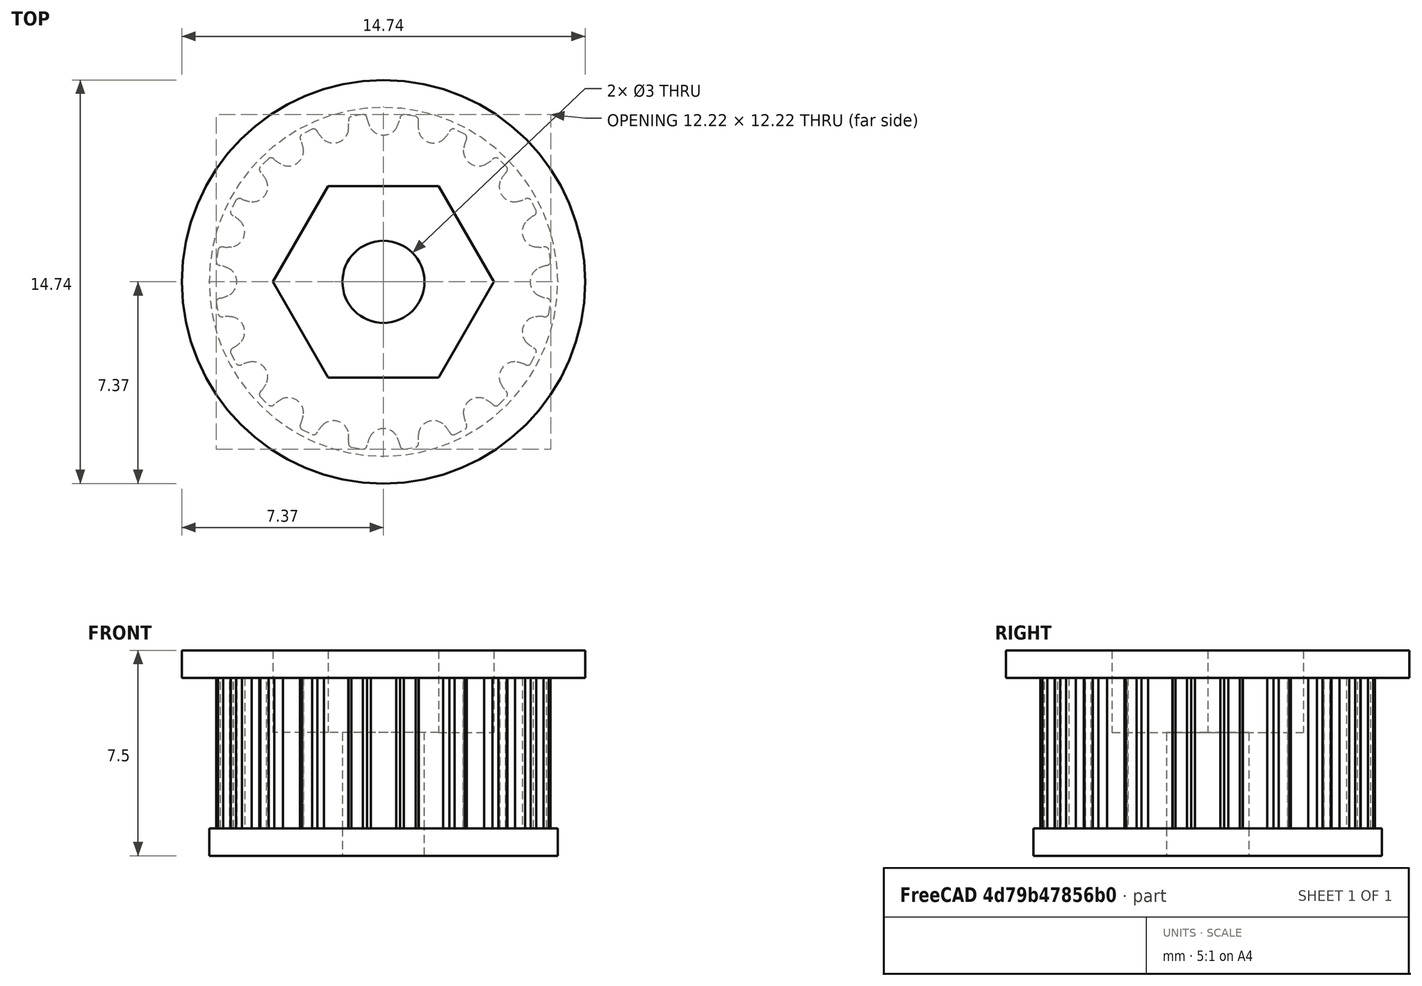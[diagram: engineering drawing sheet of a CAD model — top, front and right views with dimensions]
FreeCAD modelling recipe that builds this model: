
FCSTD DOCUMENT  (FreeCAD 0.18R16145 (Git))
Label: 20_tooth_GT2_M4_nut_hole
License: All rights reserved
LicenseURL: http://en.wikipedia.org/wiki/All_rights_reserved
objects: Sketcher::SketchObject×4, PartDesign::Pad×3, PartDesign::Pocket×1, PartDesign::Body×1
note: 13 computed .brp shape members not serialized (recipe doc carries the construction recipe); baked Part::Feature solids carry a one-line shape summary decoded from their .brp

FEATURE [Sketcher::SketchObject] SketchGear
  MapMode = 5
  Support = -> [XY_Plane]
  sketch-geometry (121):
    g0: ArcOfCircle CenterX=5.9622 CenterY=-0.75 CenterZ=0 NormalX=0 NormalY=0 NormalZ=1 AngleXU=8.1e-15 Radius=0.15 StartAngle=0 EndAngle=1.5708
    g1: ArcOfCircle CenterX=6.30816 CenterY=0.82798 CenterZ=0 NormalX=0 NormalY=0 NormalZ=-1 AngleXU=-1.3331 Radius=1.46929 StartAngle=0 EndAngle=0.255762
    g2: ArcOfCircle CenterX=5.92156 CenterY=0 CenterZ=0 NormalX=0 NormalY=0 NormalZ=-1 AngleXU=-0.984764 Radius=0.559359 StartAngle=0 EndAngle=1.96953
    g3: ArcOfCircle CenterX=6.30816 CenterY=-0.82798 CenterZ=0 NormalX=0 NormalY=0 NormalZ=-1 AngleXU=1.07734 Radius=1.46929 StartAngle=0 EndAngle=0.255762
    g4: ArcOfCircle CenterX=5.9622 CenterY=0.75 CenterZ=0 NormalX=0 NormalY=0 NormalZ=1 AngleXU=-1.5708 Radius=0.15 StartAngle=0 EndAngle=1.5708
    g5: LineSegment StartX=6.1122 StartY=0.75 StartZ=0 EndX=6.04481 EndY=1.17548 EndZ=0
    g6: ArcOfCircle CenterX=5.90215 CenterY=1.12913 CenterZ=0 NormalX=0 NormalY=0 NormalZ=1 AngleXU=0.314159 Radius=0.15 StartAngle=0 EndAngle=1.5708
    g7: ArcOfCircle CenterX=5.74356 CenterY=2.73679 CenterZ=0 NormalX=0 NormalY=0 NormalZ=-1 AngleXU=-1.64726 Radius=1.46929 StartAngle=0 EndAngle=0.255762
    g8: ArcOfCircle CenterX=5.63174 CenterY=1.82986 CenterZ=0 NormalX=0 NormalY=0 NormalZ=-1 AngleXU=-1.29892 Radius=0.559359 StartAngle=0 EndAngle=1.96953
    g9: ArcOfCircle CenterX=6.25528 CenterY=1.16187 CenterZ=0 NormalX=0 NormalY=0 NormalZ=-1 AngleXU=0.763178 Radius=1.46929 StartAngle=0 EndAngle=0.255762
    g10: ArcOfCircle CenterX=5.43862 CenterY=2.55571 CenterZ=0 NormalX=0 NormalY=0 NormalZ=1 AngleXU=-1.25664 Radius=0.15 StartAngle=0 EndAngle=1.5708
    g11: LineSegment StartX=5.58128 StartY=2.60207 StartZ=0 EndX=5.38571 EndY=2.9859 EndZ=0
    g12: ArcOfCircle CenterX=5.26436 CenterY=2.89773 CenterZ=0 NormalX=0 NormalY=0 NormalZ=1 AngleXU=0.628319 Radius=0.15 StartAngle=0 EndAngle=1.5708
    g13: ArcOfCircle CenterX=4.61674 CenterY=4.3777 CenterZ=0 NormalX=0 NormalY=0 NormalZ=-1 AngleXU=-1.96142 Radius=1.46929 StartAngle=0 EndAngle=0.255762
    g14: ArcOfCircle CenterX=4.79064 CenterY=3.4806 CenterZ=0 NormalX=0 NormalY=0 NormalZ=-1 AngleXU=-1.61308 Radius=0.559359 StartAngle=0 EndAngle=1.96953
    g15: ArcOfCircle CenterX=5.59009 CenterY=3.038 CenterZ=0 NormalX=0 NormalY=0 NormalZ=-1 AngleXU=0.449019 Radius=1.46929 StartAngle=0 EndAngle=0.255762
    g16: ArcOfCircle CenterX=4.38268 CenterY=4.11125 CenterZ=0 NormalX=0 NormalY=0 NormalZ=1 AngleXU=-0.942478 Radius=0.15 StartAngle=0 EndAngle=1.5708
    g17: LineSegment StartX=4.50403 StartY=4.19942 StartZ=0 EndX=4.19942 EndY=4.50403 EndZ=0
    g18: ArcOfCircle CenterX=4.11125 CenterY=4.38268 CenterZ=0 NormalX=0 NormalY=0 NormalZ=1 AngleXU=0.942478 Radius=0.15 StartAngle=0 EndAngle=1.5708
    g19: ArcOfCircle CenterX=3.038 CenterY=5.59009 CenterZ=0 NormalX=0 NormalY=0 NormalZ=-1 AngleXU=-2.27558 Radius=1.46929 StartAngle=0 EndAngle=0.255762
    g20: ArcOfCircle CenterX=3.4806 CenterY=4.79064 CenterZ=0 NormalX=0 NormalY=0 NormalZ=-1 AngleXU=-1.92724 Radius=0.559359 StartAngle=0 EndAngle=1.96953
    g21: ArcOfCircle CenterX=4.3777 CenterY=4.61674 CenterZ=0 NormalX=0 NormalY=0 NormalZ=-1 AngleXU=0.13486 Radius=1.46929 StartAngle=0 EndAngle=0.255762
    g22: ArcOfCircle CenterX=2.89773 CenterY=5.26436 CenterZ=0 NormalX=0 NormalY=0 NormalZ=1 AngleXU=-0.628319 Radius=0.15 StartAngle=0 EndAngle=1.5708
    g23: LineSegment StartX=2.9859 StartY=5.38571 StartZ=0 EndX=2.60207 EndY=5.58128 EndZ=0
    g24: ArcOfCircle CenterX=2.55571 CenterY=5.43862 CenterZ=0 NormalX=0 NormalY=0 NormalZ=1 AngleXU=1.25664 Radius=0.15 StartAngle=0 EndAngle=1.5708
    g25: ArcOfCircle CenterX=1.16187 CenterY=6.25528 CenterZ=0 NormalX=0 NormalY=0 NormalZ=-1 AngleXU=-2.58974 Radius=1.46929 StartAngle=0 EndAngle=0.255762
    g26: ArcOfCircle CenterX=1.82986 CenterY=5.63174 CenterZ=0 NormalX=0 NormalY=0 NormalZ=-1 AngleXU=-2.2414 Radius=0.559359 StartAngle=0 EndAngle=1.96953
    g27: ArcOfCircle CenterX=2.73679 CenterY=5.74356 CenterZ=0 NormalX=0 NormalY=0 NormalZ=-1 AngleXU=-0.1793 Radius=1.46929 StartAngle=0 EndAngle=0.255762
    g28: ArcOfCircle CenterX=1.12913 CenterY=5.90215 CenterZ=0 NormalX=0 NormalY=0 NormalZ=1 AngleXU=-0.314159 Radius=0.15 StartAngle=0 EndAngle=1.5708
    g29: LineSegment StartX=1.17548 StartY=6.04481 StartZ=0 EndX=0.75 EndY=6.1122 EndZ=0
    g30: ArcOfCircle CenterX=0.75 CenterY=5.9622 CenterZ=0 NormalX=0 NormalY=0 NormalZ=1 AngleXU=1.5708 Radius=0.15 StartAngle=0 EndAngle=1.5708
    g31: ArcOfCircle CenterX=-0.82798 CenterY=6.30816 CenterZ=0 NormalX=0 NormalY=0 NormalZ=-1 AngleXU=-2.9039 Radius=1.46929 StartAngle=0 EndAngle=0.255762
    g32: ArcOfCircle CenterX=3e-16 CenterY=5.92156 CenterZ=0 NormalX=0 NormalY=0 NormalZ=-1 AngleXU=-2.55556 Radius=0.559359 StartAngle=0 EndAngle=1.96953
    g33: ArcOfCircle CenterX=0.82798 CenterY=6.30816 CenterZ=0 NormalX=0 NormalY=0 NormalZ=-1 AngleXU=-0.493459 Radius=1.46929 StartAngle=0 EndAngle=0.255762
    g34: ArcOfCircle CenterX=-0.75 CenterY=5.9622 CenterZ=0 NormalX=0 NormalY=0 NormalZ=1 AngleXU=5.9e-15 Radius=0.15 StartAngle=0 EndAngle=1.5708
    g35: LineSegment StartX=-0.75 StartY=6.1122 StartZ=0 EndX=-1.17548 EndY=6.04481 EndZ=0
    g36: ArcOfCircle CenterX=-1.12913 CenterY=5.90215 CenterZ=0 NormalX=0 NormalY=0 NormalZ=1 AngleXU=1.88496 Radius=0.15 StartAngle=0 EndAngle=1.5708
    g37: ArcOfCircle CenterX=-2.73679 CenterY=5.74356 CenterZ=0 NormalX=0 NormalY=0 NormalZ=-1 AngleXU=3.06513 Radius=1.46929 StartAngle=0 EndAngle=0.255762
    g38: ArcOfCircle CenterX=-1.82986 CenterY=5.63174 CenterZ=0 NormalX=0 NormalY=0 NormalZ=-1 AngleXU=-2.86972 Radius=0.559359 StartAngle=0 EndAngle=1.96953
    g39: ArcOfCircle CenterX=-1.16187 CenterY=6.25528 CenterZ=0 NormalX=0 NormalY=0 NormalZ=-1 AngleXU=-0.807618 Radius=1.46929 StartAngle=0 EndAngle=0.255762
    g40: ArcOfCircle CenterX=-2.55571 CenterY=5.43862 CenterZ=0 NormalX=0 NormalY=0 NormalZ=1 AngleXU=0.314159 Radius=0.15 StartAngle=0 EndAngle=1.5708
    g41: LineSegment StartX=-2.60207 StartY=5.58128 StartZ=0 EndX=-2.9859 EndY=5.38571 EndZ=0
    g42: ArcOfCircle CenterX=-2.89773 CenterY=5.26436 CenterZ=0 NormalX=0 NormalY=0 NormalZ=1 AngleXU=2.19911 Radius=0.15 StartAngle=0 EndAngle=1.5708
    g43: ArcOfCircle CenterX=-4.3777 CenterY=4.61674 CenterZ=0 NormalX=0 NormalY=0 NormalZ=-1 AngleXU=2.75097 Radius=1.46929 StartAngle=0 EndAngle=0.255762
    g44: ArcOfCircle CenterX=-3.4806 CenterY=4.79064 CenterZ=0 NormalX=0 NormalY=0 NormalZ=-1 AngleXU=3.09931 Radius=0.559359 StartAngle=0 EndAngle=1.96953
    g45: ArcOfCircle CenterX=-3.038 CenterY=5.59009 CenterZ=0 NormalX=0 NormalY=0 NormalZ=-1 AngleXU=-1.12178 Radius=1.46929 StartAngle=0 EndAngle=0.255762
    g46: ArcOfCircle CenterX=-4.11125 CenterY=4.38268 CenterZ=0 NormalX=0 NormalY=0 NormalZ=1 AngleXU=0.628319 Radius=0.15 StartAngle=0 EndAngle=1.5708
    g47: LineSegment StartX=-4.19942 StartY=4.50403 StartZ=0 EndX=-4.50403 EndY=4.19942 EndZ=0
    g48: ArcOfCircle CenterX=-4.38268 CenterY=4.11125 CenterZ=0 NormalX=0 NormalY=0 NormalZ=1 AngleXU=2.51327 Radius=0.15 StartAngle=0 EndAngle=1.5708
    g49: ArcOfCircle CenterX=-5.59009 CenterY=3.038 CenterZ=0 NormalX=0 NormalY=0 NormalZ=-1 AngleXU=2.43681 Radius=1.46929 StartAngle=0 EndAngle=0.255762
    g50: ArcOfCircle CenterX=-4.79064 CenterY=3.4806 CenterZ=0 NormalX=0 NormalY=0 NormalZ=-1 AngleXU=2.78515 Radius=0.559359 StartAngle=0 EndAngle=1.96953
    g51: ArcOfCircle CenterX=-4.61674 CenterY=4.3777 CenterZ=0 NormalX=0 NormalY=0 NormalZ=-1 AngleXU=-1.43594 Radius=1.46929 StartAngle=0 EndAngle=0.255762
    g52: ArcOfCircle CenterX=-5.26436 CenterY=2.89773 CenterZ=0 NormalX=0 NormalY=0 NormalZ=1 AngleXU=0.942478 Radius=0.15 StartAngle=0 EndAngle=1.5708
    g53: LineSegment StartX=-5.38571 StartY=2.9859 StartZ=0 EndX=-5.58128 EndY=2.60207 EndZ=0
    g54: ArcOfCircle CenterX=-5.43862 CenterY=2.55571 CenterZ=0 NormalX=0 NormalY=0 NormalZ=1 AngleXU=2.82743 Radius=0.15 StartAngle=0 EndAngle=1.5708
    g55: ArcOfCircle CenterX=-6.25528 CenterY=1.16187 CenterZ=0 NormalX=0 NormalY=0 NormalZ=-1 AngleXU=2.12265 Radius=1.46929 StartAngle=0 EndAngle=0.255762
    g56: ArcOfCircle CenterX=-5.63174 CenterY=1.82986 CenterZ=0 NormalX=0 NormalY=0 NormalZ=-1 AngleXU=2.47099 Radius=0.559359 StartAngle=0 EndAngle=1.96953
    g57: ArcOfCircle CenterX=-5.74356 CenterY=2.73679 CenterZ=0 NormalX=0 NormalY=0 NormalZ=-1 AngleXU=-1.7501 Radius=1.46929 StartAngle=0 EndAngle=0.255762
    g58: ArcOfCircle CenterX=-5.90215 CenterY=1.12913 CenterZ=0 NormalX=0 NormalY=0 NormalZ=1 AngleXU=1.25664 Radius=0.15 StartAngle=0 EndAngle=1.5708
    g59: LineSegment StartX=-6.04481 StartY=1.17548 StartZ=0 EndX=-6.1122 EndY=0.75 EndZ=0
    g60: ArcOfCircle CenterX=-5.9622 CenterY=0.75 CenterZ=0 NormalX=0 NormalY=0 NormalZ=1 AngleXU=-3.14159 Radius=0.15 StartAngle=0 EndAngle=1.5708
    g61: ArcOfCircle CenterX=-6.30816 CenterY=-0.82798 CenterZ=0 NormalX=0 NormalY=0 NormalZ=-1 AngleXU=1.80849 Radius=1.46929 StartAngle=0 EndAngle=0.255762
    g62: ArcOfCircle CenterX=-5.92156 CenterY=7e-16 CenterZ=0 NormalX=0 NormalY=0 NormalZ=-1 AngleXU=2.15683 Radius=0.559359 StartAngle=0 EndAngle=1.96953
    g63: ArcOfCircle CenterX=-6.30816 CenterY=0.82798 CenterZ=0 NormalX=0 NormalY=0 NormalZ=-1 AngleXU=-2.06426 Radius=1.46929 StartAngle=0 EndAngle=0.255762
    g64: ArcOfCircle CenterX=-5.9622 CenterY=-0.75 CenterZ=0 NormalX=0 NormalY=0 NormalZ=1 AngleXU=1.5708 Radius=0.15 StartAngle=0 EndAngle=1.5708
    g65: LineSegment StartX=-6.1122 StartY=-0.75 StartZ=0 EndX=-6.04481 EndY=-1.17548 EndZ=0
    g66: ArcOfCircle CenterX=-5.90215 CenterY=-1.12913 CenterZ=0 NormalX=0 NormalY=0 NormalZ=1 AngleXU=-2.82743 Radius=0.15 StartAngle=0 EndAngle=1.5708
    g67: ArcOfCircle CenterX=-5.74356 CenterY=-2.73679 CenterZ=0 NormalX=0 NormalY=0 NormalZ=-1 AngleXU=1.49433 Radius=1.46929 StartAngle=0 EndAngle=0.255762
    g68: ArcOfCircle CenterX=-5.63174 CenterY=-1.82986 CenterZ=0 NormalX=0 NormalY=0 NormalZ=-1 AngleXU=1.84267 Radius=0.559359 StartAngle=0 EndAngle=1.96953
    g69: ArcOfCircle CenterX=-6.25528 CenterY=-1.16187 CenterZ=0 NormalX=0 NormalY=0 NormalZ=-1 AngleXU=-2.37841 Radius=1.46929 StartAngle=0 EndAngle=0.255762
    g70: ArcOfCircle CenterX=-5.43862 CenterY=-2.55571 CenterZ=0 NormalX=0 NormalY=0 NormalZ=1 AngleXU=1.88496 Radius=0.15 StartAngle=0 EndAngle=1.5708
    g71: LineSegment StartX=-5.58128 StartY=-2.60207 StartZ=0 EndX=-5.38571 EndY=-2.9859 EndZ=0
    g72: ArcOfCircle CenterX=-5.26436 CenterY=-2.89773 CenterZ=0 NormalX=0 NormalY=0 NormalZ=1 AngleXU=-2.51327 Radius=0.15 StartAngle=0 EndAngle=1.5708
    g73: ArcOfCircle CenterX=-4.61674 CenterY=-4.3777 CenterZ=0 NormalX=0 NormalY=0 NormalZ=-1 AngleXU=1.18017 Radius=1.46929 StartAngle=0 EndAngle=0.255762
    g74: ArcOfCircle CenterX=-4.79064 CenterY=-3.4806 CenterZ=0 NormalX=0 NormalY=0 NormalZ=-1 AngleXU=1.52851 Radius=0.559359 StartAngle=0 EndAngle=1.96953
    g75: ArcOfCircle CenterX=-5.59009 CenterY=-3.038 CenterZ=0 NormalX=0 NormalY=0 NormalZ=-1 AngleXU=-2.69257 Radius=1.46929 StartAngle=0 EndAngle=0.255762
    g76: ArcOfCircle CenterX=-4.38268 CenterY=-4.11125 CenterZ=0 NormalX=0 NormalY=0 NormalZ=1 AngleXU=2.19911 Radius=0.15 StartAngle=0 EndAngle=1.5708
    g77: LineSegment StartX=-4.50403 StartY=-4.19942 StartZ=0 EndX=-4.19942 EndY=-4.50403 EndZ=0
    g78: ArcOfCircle CenterX=-4.11125 CenterY=-4.38268 CenterZ=0 NormalX=0 NormalY=0 NormalZ=1 AngleXU=-2.19911 Radius=0.15 StartAngle=0 EndAngle=1.5708
    g79: ArcOfCircle CenterX=-3.038 CenterY=-5.59009 CenterZ=0 NormalX=0 NormalY=0 NormalZ=-1 AngleXU=0.866016 Radius=1.46929 StartAngle=0 EndAngle=0.255762
    g80: ArcOfCircle CenterX=-3.4806 CenterY=-4.79064 CenterZ=0 NormalX=0 NormalY=0 NormalZ=-1 AngleXU=1.21435 Radius=0.559359 StartAngle=0 EndAngle=1.96953
    g81: ArcOfCircle CenterX=-4.3777 CenterY=-4.61674 CenterZ=0 NormalX=0 NormalY=0 NormalZ=-1 AngleXU=-3.00673 Radius=1.46929 StartAngle=0 EndAngle=0.255762
    g82: ArcOfCircle CenterX=-2.89773 CenterY=-5.26436 CenterZ=0 NormalX=0 NormalY=0 NormalZ=1 AngleXU=2.51327 Radius=0.15 StartAngle=0 EndAngle=1.5708
    g83: LineSegment StartX=-2.9859 StartY=-5.38571 StartZ=0 EndX=-2.60207 EndY=-5.58128 EndZ=0
    g84: ArcOfCircle CenterX=-2.55571 CenterY=-5.43862 CenterZ=0 NormalX=0 NormalY=0 NormalZ=1 AngleXU=-1.88496 Radius=0.15 StartAngle=0 EndAngle=1.5708
    g85: ArcOfCircle CenterX=-1.16187 CenterY=-6.25528 CenterZ=0 NormalX=0 NormalY=0 NormalZ=-1 AngleXU=0.551856 Radius=1.46929 StartAngle=0 EndAngle=0.255762
    g86: ArcOfCircle CenterX=-1.82986 CenterY=-5.63174 CenterZ=0 NormalX=0 NormalY=0 NormalZ=-1 AngleXU=0.900192 Radius=0.559359 StartAngle=0 EndAngle=1.96953
    g87: ArcOfCircle CenterX=-2.73679 CenterY=-5.74356 CenterZ=0 NormalX=0 NormalY=0 NormalZ=-1 AngleXU=2.96229 Radius=1.46929 StartAngle=0 EndAngle=0.255762
    g88: ArcOfCircle CenterX=-1.12913 CenterY=-5.90215 CenterZ=0 NormalX=0 NormalY=0 NormalZ=1 AngleXU=2.82743 Radius=0.15 StartAngle=0 EndAngle=1.5708
    g89: LineSegment StartX=-1.17548 StartY=-6.04481 StartZ=0 EndX=-0.75 EndY=-6.1122 EndZ=0
    g90: ArcOfCircle CenterX=-0.75 CenterY=-5.9622 CenterZ=0 NormalX=0 NormalY=0 NormalZ=1 AngleXU=-1.5708 Radius=0.15 StartAngle=0 EndAngle=1.5708
    g91: ArcOfCircle CenterX=0.82798 CenterY=-6.30816 CenterZ=0 NormalX=0 NormalY=0 NormalZ=-1 AngleXU=0.237697 Radius=1.46929 StartAngle=0 EndAngle=0.255762
    g92: ArcOfCircle CenterX=-1e-15 CenterY=-5.92156 CenterZ=0 NormalX=0 NormalY=0 NormalZ=-1 AngleXU=0.586033 Radius=0.559359 StartAngle=0 EndAngle=1.96953
    g93: ArcOfCircle CenterX=-0.82798 CenterY=-6.30816 CenterZ=0 NormalX=0 NormalY=0 NormalZ=-1 AngleXU=2.64813 Radius=1.46929 StartAngle=0 EndAngle=0.255762
    g94: ArcOfCircle CenterX=0.75 CenterY=-5.9622 CenterZ=0 NormalX=0 NormalY=0 NormalZ=1 AngleXU=-3.14159 Radius=0.15 StartAngle=0 EndAngle=1.5708
    g95: LineSegment StartX=0.75 StartY=-6.1122 StartZ=0 EndX=1.17548 EndY=-6.04481 EndZ=0
    g96: ArcOfCircle CenterX=1.12913 CenterY=-5.90215 CenterZ=0 NormalX=0 NormalY=0 NormalZ=1 AngleXU=-1.25664 Radius=0.15 StartAngle=0 EndAngle=1.5708
    g97: ArcOfCircle CenterX=2.73679 CenterY=-5.74356 CenterZ=0 NormalX=0 NormalY=0 NormalZ=-1 AngleXU=-0.0764622 Radius=1.46929 StartAngle=0 EndAngle=0.255762
    g98: ArcOfCircle CenterX=1.82986 CenterY=-5.63174 CenterZ=0 NormalX=0 NormalY=0 NormalZ=-1 AngleXU=0.271874 Radius=0.559359 StartAngle=0 EndAngle=1.96953
    g99: ArcOfCircle CenterX=1.16187 CenterY=-6.25528 CenterZ=0 NormalX=0 NormalY=0 NormalZ=-1 AngleXU=2.33397 Radius=1.46929 StartAngle=0 EndAngle=0.255762
    g100: ArcOfCircle CenterX=2.55571 CenterY=-5.43862 CenterZ=0 NormalX=0 NormalY=0 NormalZ=1 AngleXU=-2.82743 Radius=0.15 StartAngle=0 EndAngle=1.5708
    g101: LineSegment StartX=2.60207 StartY=-5.58128 StartZ=0 EndX=2.9859 EndY=-5.38571 EndZ=0
    g102: ArcOfCircle CenterX=2.89773 CenterY=-5.26436 CenterZ=0 NormalX=0 NormalY=0 NormalZ=1 AngleXU=-0.942478 Radius=0.15 StartAngle=0 EndAngle=1.5708
    g103: ArcOfCircle CenterX=4.3777 CenterY=-4.61674 CenterZ=0 NormalX=0 NormalY=0 NormalZ=-1 AngleXU=-0.390621 Radius=1.46929 StartAngle=0 EndAngle=0.255762
    g104: ArcOfCircle CenterX=3.4806 CenterY=-4.79064 CenterZ=0 NormalX=0 NormalY=0 NormalZ=-1 AngleXU=-0.0422858 Radius=0.559359 StartAngle=0 EndAngle=1.96953
    g105: ArcOfCircle CenterX=3.038 CenterY=-5.59009 CenterZ=0 NormalX=0 NormalY=0 NormalZ=-1 AngleXU=2.01982 Radius=1.46929 StartAngle=0 EndAngle=0.255762
    g106: ArcOfCircle CenterX=4.11125 CenterY=-4.38268 CenterZ=0 NormalX=0 NormalY=0 NormalZ=1 AngleXU=-2.51327 Radius=0.15 StartAngle=0 EndAngle=1.5708
    g107: LineSegment StartX=4.19942 StartY=-4.50403 StartZ=0 EndX=4.50403 EndY=-4.19942 EndZ=0
    g108: ArcOfCircle CenterX=4.38268 CenterY=-4.11125 CenterZ=0 NormalX=0 NormalY=0 NormalZ=1 AngleXU=-0.628319 Radius=0.15 StartAngle=0 EndAngle=1.5708
    g109: ArcOfCircle CenterX=5.59009 CenterY=-3.038 CenterZ=0 NormalX=0 NormalY=0 NormalZ=-1 AngleXU=-0.704781 Radius=1.46929 StartAngle=0 EndAngle=0.255762
    g110: ArcOfCircle CenterX=4.79064 CenterY=-3.4806 CenterZ=0 NormalX=0 NormalY=0 NormalZ=-1 AngleXU=-0.356445 Radius=0.559359 StartAngle=0 EndAngle=1.96953
    g111: ArcOfCircle CenterX=4.61674 CenterY=-4.3777 CenterZ=0 NormalX=0 NormalY=0 NormalZ=-1 AngleXU=1.70566 Radius=1.46929 StartAngle=0 EndAngle=0.255762
    g112: ArcOfCircle CenterX=5.26436 CenterY=-2.89773 CenterZ=0 NormalX=0 NormalY=0 NormalZ=1 AngleXU=-2.19911 Radius=0.15 StartAngle=0 EndAngle=1.5708
    g113: LineSegment StartX=5.38571 StartY=-2.9859 StartZ=0 EndX=5.58128 EndY=-2.60207 EndZ=0
    g114: ArcOfCircle CenterX=5.43862 CenterY=-2.55571 CenterZ=0 NormalX=0 NormalY=0 NormalZ=1 AngleXU=-0.314159 Radius=0.15 StartAngle=0 EndAngle=1.5708
    g115: ArcOfCircle CenterX=6.25528 CenterY=-1.16187 CenterZ=0 NormalX=0 NormalY=0 NormalZ=-1 AngleXU=-1.01894 Radius=1.46929 StartAngle=0 EndAngle=0.255762
    g116: ArcOfCircle CenterX=5.63174 CenterY=-1.82986 CenterZ=0 NormalX=0 NormalY=0 NormalZ=-1 AngleXU=-0.670604 Radius=0.559359 StartAngle=0 EndAngle=1.96953
    g117: ArcOfCircle CenterX=5.74356 CenterY=-2.73679 CenterZ=0 NormalX=0 NormalY=0 NormalZ=-1 AngleXU=1.3915 Radius=1.46929 StartAngle=0 EndAngle=0.255762
    g118: ArcOfCircle CenterX=5.90215 CenterY=-1.12913 CenterZ=0 NormalX=0 NormalY=0 NormalZ=1 AngleXU=-1.88496 Radius=0.15 StartAngle=0 EndAngle=1.5708
    g119: LineSegment StartX=6.04481 StartY=-1.17548 StartZ=0 EndX=6.1122 EndY=-0.75 EndZ=0
    g120: Circle CenterX=0 CenterY=0 CenterZ=0 NormalX=0 NormalY=0 NormalZ=1 AngleXU=0 Radius=1.5
FEATURE [PartDesign::Pad] Pad
  Length = 6.5
  Length2 = 100
  Profile = -> SketchGear
  Type = 0
FEATURE [Sketcher::SketchObject] SketchBase
  MapMode = 5
  Support = -> [XY_Plane]
  sketch-geometry (2):
    g0: Circle CenterX=0 CenterY=0 CenterZ=0 NormalX=0 NormalY=0 NormalZ=1 AngleXU=0 Radius=6.37
    g1: Circle CenterX=0 CenterY=0 CenterZ=0 NormalX=0 NormalY=0 NormalZ=1 AngleXU=0 Radius=1.5
FEATURE [PartDesign::Pad] PadBase
  BaseFeature = -> Pad
  Length = 1
  Length2 = 100
  Profile = -> SketchBase
  Type = 0
FEATURE [Sketcher::SketchObject] SketchTop
  MapMode = 5
  Placement = pos=(0,0,6.5) rot=(0,0,1;0rad)
  sketch-geometry (2):
    g0: Circle CenterX=0 CenterY=0 CenterZ=0 NormalX=0 NormalY=0 NormalZ=1 AngleXU=0 Radius=7.37
    g1: Circle CenterX=0 CenterY=0 CenterZ=0 NormalX=0 NormalY=0 NormalZ=1 AngleXU=0 Radius=1.5
FEATURE [PartDesign::Pad] PadTop
  BaseFeature = -> PadBase
  Length = 1
  Length2 = 100
  Profile = -> SketchTop
  Type = 0
FEATURE [Sketcher::SketchObject] Sketch
  MapMode = 5
  Placement = pos=(0,0,7.5) rot=(0,0,1;0rad)
  Support = -> [PadTop]
  sketch-geometry (7):
    g0: LineSegment StartX=2.02073 StartY=-3.5 StartZ=0 EndX=4.04145 EndY=-3.6e-15 EndZ=0
    g1: LineSegment StartX=4.04145 StartY=-3.6e-15 StartZ=0 EndX=2.02073 EndY=3.5 EndZ=0
    g2: LineSegment StartX=2.02073 StartY=3.5 StartZ=0 EndX=-2.02073 EndY=3.5 EndZ=0
    g3: LineSegment StartX=-2.02073 StartY=3.5 StartZ=0 EndX=-4.04145 EndY=-9e-16 EndZ=0
    g4: LineSegment StartX=-4.04145 StartY=-1.1e-15 StartZ=0 EndX=-2.02073 EndY=-3.5 EndZ=0
    g5: LineSegment StartX=-2.02073 StartY=-3.5 StartZ=0 EndX=2.02073 EndY=-3.5 EndZ=0
    g6: Circle [constr] CenterX=0 CenterY=0 CenterZ=0 NormalX=0 NormalY=0 NormalZ=1 AngleXU=0 Radius=4.04145
  constraints (16):
    c: Coincident(g0,g1)
    c: Coincident(g1,g2)
    c: Coincident(g2,g3)
    c: Coincident(g3,g4)
    c: Coincident(g4,g5)
    c: Coincident(g5,g0)
    c: Equal(g0, g1-g5) x5
    c: PointOnObject(g0,g6)
    c: PointOnObject(g1,g6)
    c: PointOnObject(g2,g6)
    c: PointOnObject(g3,g6)
    c: PointOnObject(g4,g6)
    c: PointOnObject(g5,g6)
    c: Coincident(g6,g-1)
    c: Horizontal(g5)
    c: DistanceY(g0,g1) = 7
FEATURE [PartDesign::Pocket] Pocket
  BaseFeature = -> PadTop
  Length = 3
  Length2 = 100
  Profile = -> Sketch
  Type = 0
FEATURE [PartDesign::Body] Gear
  Group = -> [SketchGear,Pad,SketchBase,PadBase,SketchTop,PadTop,Sketch,Pocket]
  Origin = -> Origin
  Tip = -> Pocket
